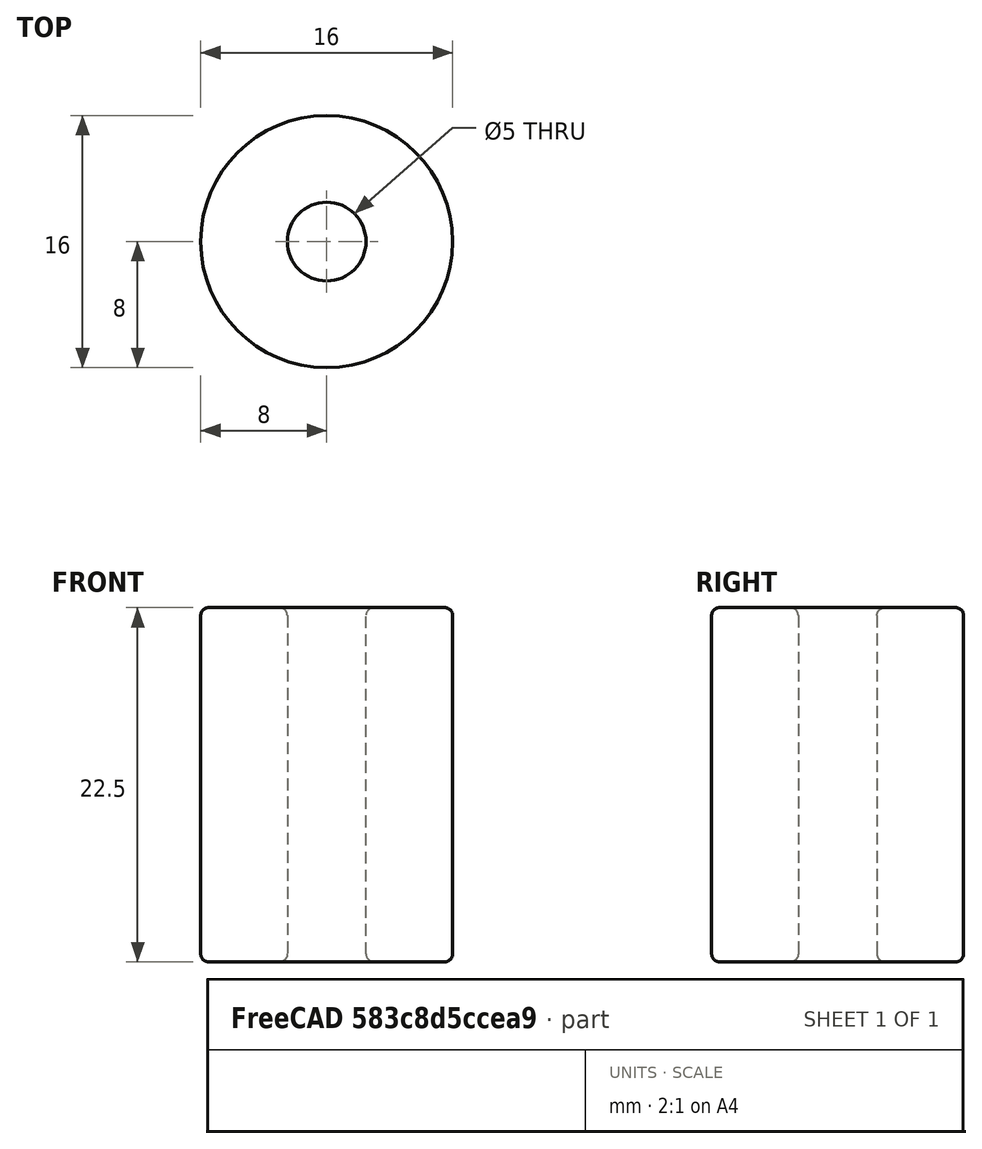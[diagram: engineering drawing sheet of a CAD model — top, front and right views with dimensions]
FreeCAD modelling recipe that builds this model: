
FCSTD DOCUMENT  (FreeCAD 0.17R8934 (Git))
Label: z_coupler
License: All rights reserved
LicenseURL: http://en.wikipedia.org/wiki/All_rights_reserved
objects: Sketcher::SketchObject×1, PartDesign::Pad×1, PartDesign::Fillet×1, PartDesign::Body×1, Part::Feature×1
note: 6 computed .brp shape members not serialized (recipe doc carries the construction recipe); baked Part::Feature solids carry a one-line shape summary decoded from their .brp

FEATURE [Sketcher::SketchObject] Sketch
  MapMode = 5
  Support = -> [XY_Plane]
  sketch-geometry (2):
    g0: Circle CenterX=0 CenterY=0 CenterZ=0 NormalX=0 NormalY=0 NormalZ=1 Radius=8
    g1: Circle CenterX=0 CenterY=0 CenterZ=0 NormalX=0 NormalY=0 NormalZ=1 Radius=2.5
  constraints (4):
    c: Coincident(g0,g-1)
    c: Radius(g0) = 8
    c: Coincident(g0,g1)
    c: Radius(g1) = 2.5
FEATURE [PartDesign::Pad] Pad
  Length = 22.5
  Length2 = 100
  Profile = -> Sketch
  Type = 0
FEATURE [PartDesign::Fillet] Fillet
  Base = -> Pad [Edge3,Edge2,Edge6,Edge5]
  BaseFeature = -> Pad
  Radius = 0.5
FEATURE [PartDesign::Body] Body
  Model = -> [Sketch,Pad,Fillet]
  Origin = -> BodyOrigin
FEATURE [Part::Feature] Fillet001
  shape: bbox 17.32 x 17.32 x 22.5 mm, 8 faces (baked)
